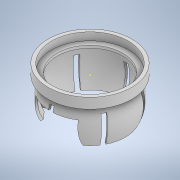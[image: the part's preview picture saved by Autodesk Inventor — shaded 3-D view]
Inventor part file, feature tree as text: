
AUTODESK INVENTOR PART (.ipt)
format: ipt  version: 2022 (Build 260153000, 153)  size: 224,768 bytes
history: native  units: in
note: dims shown in document units (in); Inventor stores cm internally (conversion verified against a paired STEP export)
features: other x3, sketch x3, extrude x2
ambient origin geometry x8: Origin, YZ Plane, XZ Plane, XY Plane, X Axis, Y Axis, Z Axis, Center Point
bodies: Solid1 (feature_tree)
feature tree (8):
  other  "cam-socket-try1.ipt"
  sketch  "Sketch1"  dims[d0=0.3937in d2=3.8228in]
  extrude  "Extrusion1"  Depth=0.3937in
  extrude  "Extrusion2"  Depth=0.1181in
  other  "Solid1::cam-socket-try1.ipt"
  other  "TaggingFeature1"
  sketch  "Sketch2"  dims[d3=0.1181in d4=0.0in d5=0.1575in]
  sketch  "Sketch3"  dims[d6=0.3543in d7=0.0in]
